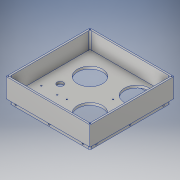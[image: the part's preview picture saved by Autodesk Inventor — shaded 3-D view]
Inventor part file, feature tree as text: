
AUTODESK INVENTOR PART (.ipt)
format: ipt  version: 2018 (Build 220112000, 112)  size: 313,344 bytes
history: native  units: in
note: dims shown in document units (in); Inventor stores cm internally (conversion verified against a paired STEP export)
features: thread x24, sketch x7, extrude x4, hole x4, projected_geometry x2, fillet x1
ambient origin geometry x8: Origin, YZ Plane, XZ Plane, XY Plane, X Axis, Y Axis, Z Axis, Center Point
bodies: Solid1 (feature_tree)
feature tree (42):
  extrude  "Extrusion1"  Depth=7.874in
  extrude  "Extrusion2"  Depth=7.5591in
  extrude  "Extrusion3"  Depth=0.1575in
  fillet  "Fillet1"  Radius=0.1575in
  extrude  "Extrusion4"  Depth=7.5591in
  hole  "Hole1"  [1 undecoded]
  hole  "Hole2"  [1 undecoded]
  hole  "Hole3"  [1 undecoded]
  hole  "Hole4"  [1 undecoded]
  thread  "Thread1"  [1 undecoded]
  thread  "Thread2"  [1 undecoded]
  thread  "Thread3"  [1 undecoded]
  thread  "Thread4"  [1 undecoded]
  thread  "Thread5"  [1 undecoded]
  thread  "Thread6"  [1 undecoded]
  thread  "Thread7"  [1 undecoded]
  thread  "Thread8"  [1 undecoded]
  thread  "Thread9"  [1 undecoded]
  thread  "Thread10"  [1 undecoded]
  thread  "Thread11"  [1 undecoded]
  thread  "Thread12"  [1 undecoded]
  thread  "Thread13"  [1 undecoded]
  thread  "Thread14"  [1 undecoded]
  thread  "Thread15"  [1 undecoded]
  thread  "Thread16"  [1 undecoded]
  thread  "Thread17"  [1 undecoded]
  thread  "Thread18"  [1 undecoded]
  thread  "Thread19"  [1 undecoded]
  thread  "Thread20"  [1 undecoded]
  thread  "Thread21"  [1 undecoded]
  thread  "Thread22"  [1 undecoded]
  thread  "Thread23"  [1 undecoded]
  thread  "Thread24"  [1 undecoded]
  sketch  "Sketch1"  dims[d0=7.874in d1=7.874in]
  sketch  "Sketch2"  dims[d2=2.2047in d3=0.0in d4=7.5591in]
  sketch  "Sketch3"  dims[d5=7.5591in d6=0.1575in d7=0.1575in]
  projected_geometry  "Projected Loop1"
  sketch  "Sketch4"  dims[d8=1.5748in d9=0.0in d10=7.5591in]
  sketch  "Sketch5"  dims[d11=7.5591in d12=0.1575in]
  projected_geometry  "Projected Loop2"
  sketch  "Sketch6"  dims[d13=0.1575in d14=0.3937in d15=0.0in]
  sketch  "Sketch8"  dims[d16=0.1575in d17=0.1575in d18=0.1181in d19=0.1181in d20=0.1181in d21=0.1181in d22=0.1181in d23=0.1181in d24=0.1181in d25=0.1181in d26=0.1181in d27=0.1181in d28=0.1181in d29=0.1181in d30=0.1181in d31=0.2362in d32=0.1575in d33=0.0787in d34=90.0deg d35=0.1969in d36=0.8108in d37=0.1575in d38=0.1969in d40=1.1811in d42=3.1496in d43=0.3937in d45=0.3937in d47=0.1575in d48=0.315in d49=0.1575in d50=0.0787in d51=90.0deg d52=0.4646in d53=0.8108in d54=0.4331in d56=1.1811in d58=0.3937in d59=0.1575in d60=0.1969in d61=3.1496in d62=0.4331in d63=0.3937in d64=0.1575in d65=0.315in d66=0.1575in d67=0.0787in d68=90.0deg d69=0.4646in d70=0.8108in d74=1.9685in d75=2.6772in d76=0.3937in d79=5.315in d80=0.4724in d81=2.6772in d82=0.4724in d83=2.6772in d84=0.1575in d85=0.1575in d86=0.1575in d87=0.1575in d88=0.5906in d89=0.5906in d90=0.5906in d91=0.5906in d92=0.2362in d93=0.2362in d94=0.2362in d95=0.2362in d96=0.1181in d97=0.2362in d98=0.1575in d99=0.0787in d100=90.0deg d101=0.1969in d102=0.8108in d103=4.7244in d104=2.5591in d105=2.5591in d106=4.3307in d107=0.1575in d108=1.5748in d110=360.0deg d112=0.3937in d113=0.0in d114=0.3937in d115=0.0in d116=0.3937in d117=0.0in d118=0.3937in d119=0.0in d120=0.3937in d121=0.0in d122=0.3937in d123=0.0in d124=0.3937in d125=0.0in d126=0.3937in d127=0.0in d128=0.3937in d129=0.0in d130=0.3937in d131=0.0in d132=0.3937in d133=0.0in d134=0.3937in d135=0.0in d136=0.3937in d137=0.0in d138=0.3937in d139=0.0in d140=0.3937in d141=0.0in d142=0.3937in d143=0.0in d144=0.3937in d145=0.0in d146=0.3937in d147=0.0in d148=0.3937in d149=0.0in d150=0.3937in d151=0.0in d152=3.1496in d153=2.5591in d154=2.5591in d155=2.9528in d156=5.5118in d157=5.5118in d158=4.3307in d159=1.9685in d160=2.6772in d161=0.3937in d162=3.937in d163=4.7244in d164=5.315in d165=1.9685in d166=1.9685in d167=0.3543in d168=2.3622in d169=2.3622in d170=2.3622in d171=0.5906in d172=0.7874in d173=0.9843in d174=1.7717in d175=6.1811in d176=0.3937in d177=0.0in d178=0.3937in d179=0.0in d180=0.3937in d181=0.0in d182=0.3937in d183=0.0in d184=0.3937in d185=0.0in]
note: 28 required parameter values undecoded (feature->parameter linkage not recoverable at this tier; creation-order binding heuristic only, values carry confidence <= 0.55)
